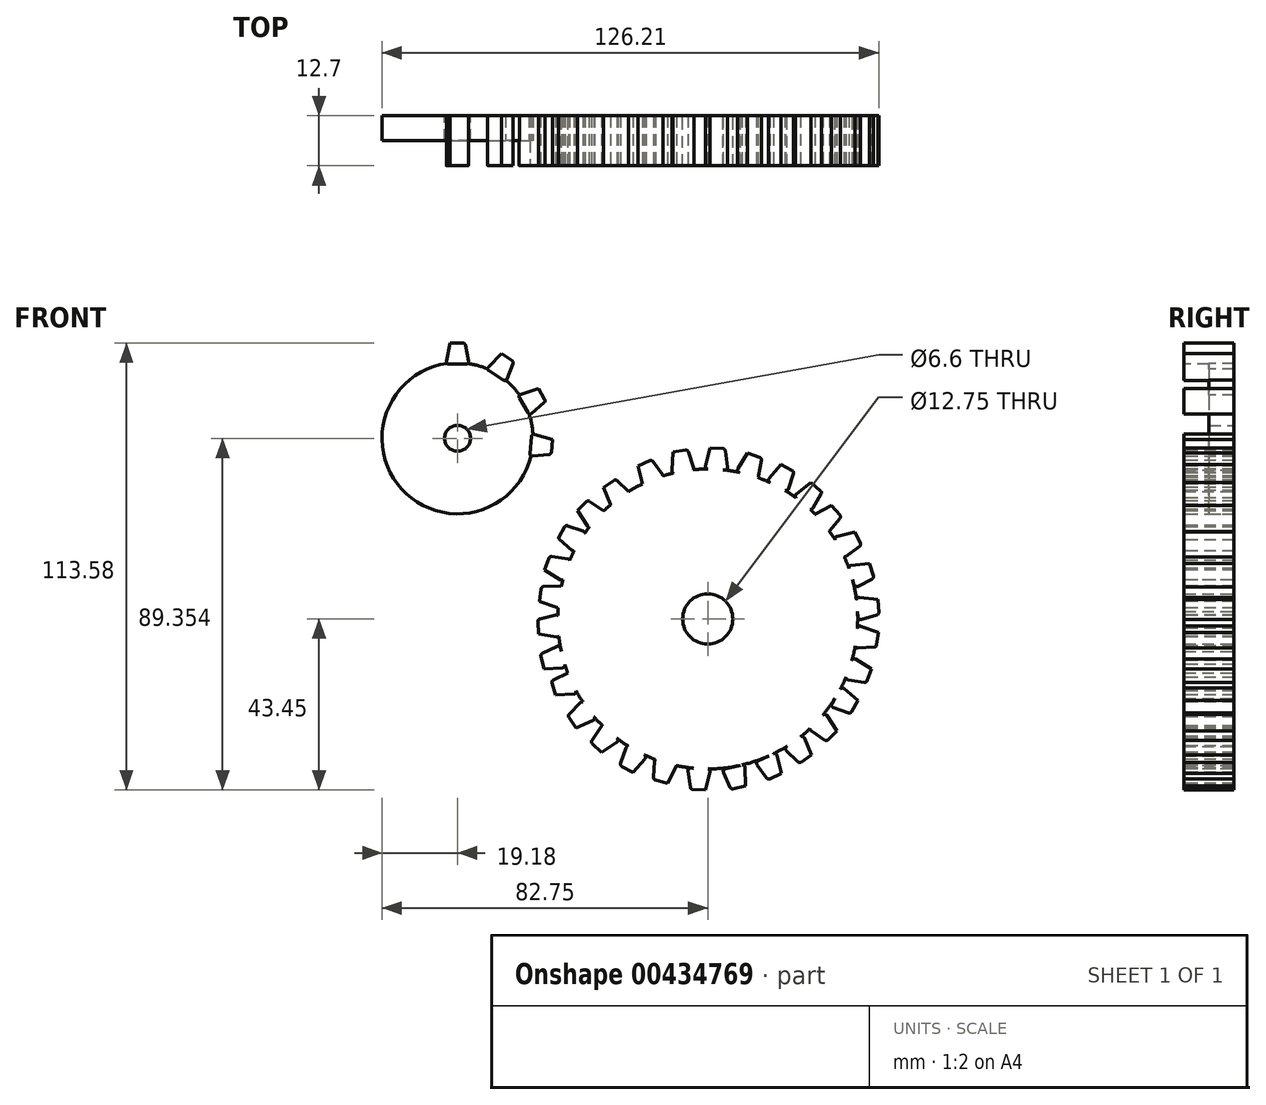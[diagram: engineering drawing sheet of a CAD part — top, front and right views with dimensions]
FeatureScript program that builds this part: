
annotation { "Feature Type Name" : "Feature", "Feature Type Description" : "" }
export const myFeature = defineFeature(function(context is Context, id is Id, definition is map)
    precondition{}
    {
        {
            var Q0;
            Q0=qCreatedBy(makeId("Front.planeOp"),FACE);
            var sketch = newSketch(context, id + "F0", { "sketchPlane" : qUnion([Q0])});
            skCircle(sketch, "E0", {"center": v(0, 0) * mm, "radius": 38.1 * mm});
            skCircle(sketch, "E1", {"center": v(0, 0) * mm, "radius": 6.37 * mm});
            skSolve(sketch);
        }
        {
            var Q0;
            Q0=makeQuery(id+"F0.imprint","IMPRINT",FACE,{"disambiguationData":[TD([[makeQuery(id+"F0.imprint","IMPRINT",EDGE,{"derivedFrom":sQuery(id+"F0.wireOp",EDGE,"E0")}),1.0]])]});
            extrude(context, id + "F1", {"entities" : qUnion([Q0]), "depth" : 12.7 * mm});
        }
        {
            var Q0;
            Q0=qCreatedBy(makeId("Front.planeOp"),FACE);
            var sketch = newSketch(context, id + "F2", { "sketchPlane" : qUnion([Q0])});
            skCircle(sketch, "E2", {"center": v(-63.57, 45.9) * mm, "radius": 19.18 * mm});
            skCircle(sketch, "E3", {"center": v(-63.57, 45.9) * mm, "radius": 3.3 * mm});
            skSolve(sketch);
        }
        {
            var Q0;
            Q0 = qSketchRegion(id + "F2", true);
            extrude(context, id + "F3", {"entities" : qUnion([Q0]), "depth" : 6.35 * mm});
        }
        {
            var Q0;
            Q0=makeQuery(id+"F1.opExtrude","CAP_FACE",FACE,{"disambiguationData":[OSD([sQuery(id+"F0.wireOp",EDGE,"E0"),sQuery(id+"F0.wireOp",EDGE,"E1")])],"isStart":false});
            var sketch = newSketch(context, id + "F4", { "sketchPlane" : qUnion([Q0])});
            skLineSegment(sketch, "E4", {"start": v(-6.97, 42.7) * mm, "end": v(-8.84, 42.45) * mm});
            skLineSegment(sketch, "E5", {"start": v(-8.84, 42.45) * mm, "end": v(-5.61, 42.9) * mm});
            skPoint(sketch, "E5.endSnap0", {"position": v(-7.9, 42.58) * mm});
            skLineSegment(sketch, "E6", {"start": v(-4.92, 42.47) * mm, "end": v(-3.6, 38.51) * mm});
            skLineSegment(sketch, "E7", {"start": v(-8.84, 42.45) * mm, "end": v(-9.14, 37.75) * mm});
            skLineSegment(sketch, "E8", {"start": v(-8.42, 37.08) * mm, "end": v(-4.1, 37.68) * mm});
            skPoint(sketch, "E9.visualSharp", {"position": v(-5.1, 42.96) * mm});
            skArc(sketch, "E9.filletArc", {"start": v(-4.92, 42.47) * mm, "mid": v(-5.2, 42.8) * mm, "end": v(-5.61, 42.9) * mm});
            skPoint(sketch, "E10.visualSharp", {"position": v(-3.35, 37.79) * mm});
            skArc(sketch, "E10.filletArc", {"start": v(-4.1, 37.68) * mm, "mid": v(-3.66, 37.98) * mm, "end": v(-3.6, 38.51) * mm});
            skPoint(sketch, "E11.visualSharp", {"position": v(-9.2, 36.97) * mm});
            skArc(sketch, "E11.filletArc", {"start": v(-9.14, 37.75) * mm, "mid": v(-8.94, 37.25) * mm, "end": v(-8.42, 37.08) * mm});
            skLineSegment(sketch, "E12", {"start": v(2.48, 43.35) * mm, "end": v(0.6, 43.45) * mm});
            skLineSegment(sketch, "E13", {"start": v(0.6, 43.45) * mm, "end": v(3.85, 43.28) * mm});
            skLineSegment(sketch, "E14", {"start": v(4.44, 42.73) * mm, "end": v(5, 38.6) * mm});
            skLineSegment(sketch, "E15", {"start": v(0.6, 43.45) * mm, "end": v(-0.58, 38.9) * mm});
            skLineSegment(sketch, "E16", {"start": v(0, 38.1) * mm, "end": v(4.35, 37.88) * mm});
            skArc(sketch, "E17.filletArc", {"start": v(4.44, 42.73) * mm, "mid": v(4.24, 43.12) * mm, "end": v(3.85, 43.28) * mm});
            skArc(sketch, "E18.filletArc", {"start": v(4.35, 37.88) * mm, "mid": v(4.85, 38.09) * mm, "end": v(5, 38.6) * mm});
            skArc(sketch, "E19.filletArc", {"start": v(-0.58, 38.9) * mm, "mid": v(-0.48, 38.36) * mm, "end": v(0, 38.1) * mm});
            skLineSegment(sketch, "E20", {"start": v(11.91, 41.54) * mm, "end": v(10.14, 42.19) * mm});
            skLineSegment(sketch, "E21", {"start": v(10.14, 42.19) * mm, "end": v(13.2, 41.08) * mm});
            skLineSegment(sketch, "E22", {"start": v(13.6, 40.38) * mm, "end": v(12.94, 36.26) * mm});
            skLineSegment(sketch, "E23", {"start": v(10.14, 42.19) * mm, "end": v(7.68, 38.18) * mm});
            skLineSegment(sketch, "E24", {"start": v(8, 37.25) * mm, "end": v(12.1, 35.77) * mm});
            skArc(sketch, "E25.filletArc", {"start": v(13.6, 40.38) * mm, "mid": v(13.53, 40.8) * mm, "end": v(13.2, 41.08) * mm});
            skArc(sketch, "E26.filletArc", {"start": v(12.1, 35.77) * mm, "mid": v(12.63, 35.81) * mm, "end": v(12.94, 36.26) * mm});
            skArc(sketch, "E27.filletArc", {"start": v(7.68, 38.18) * mm, "mid": v(7.62, 37.64) * mm, "end": v(8, 37.25) * mm});
            skLineSegment(sketch, "E28", {"start": v(27.62, 33.45) * mm, "end": v(26.18, 34.67) * mm});
            skLineSegment(sketch, "E29", {"start": v(26.18, 34.67) * mm, "end": v(28.66, 32.57) * mm});
            skLineSegment(sketch, "E30", {"start": v(28.8, 31.77) * mm, "end": v(26.76, 28.14) * mm});
            skLineSegment(sketch, "E31", {"start": v(26.18, 34.67) * mm, "end": v(22.48, 31.76) * mm});
            skLineSegment(sketch, "E32", {"start": v(22.47, 30.77) * mm, "end": v(25.8, 27.97) * mm});
            skArc(sketch, "E33.filletArc", {"start": v(28.8, 31.77) * mm, "mid": v(28.88, 32.2) * mm, "end": v(28.66, 32.57) * mm});
            skArc(sketch, "E34.filletArc", {"start": v(25.8, 27.97) * mm, "mid": v(26.32, 27.83) * mm, "end": v(26.76, 28.14) * mm});
            skArc(sketch, "E35.filletArc", {"start": v(22.48, 31.76) * mm, "mid": v(22.24, 31.27) * mm, "end": v(22.47, 30.77) * mm});
            skLineSegment(sketch, "E36", {"start": v(32.68, 27.4) * mm, "end": v(31.47, 28.85) * mm});
            skLineSegment(sketch, "E37", {"start": v(31.47, 28.85) * mm, "end": v(33.56, 26.36) * mm});
            skLineSegment(sketch, "E38", {"start": v(33.57, 25.55) * mm, "end": v(30.93, 22.32) * mm});
            skLineSegment(sketch, "E39", {"start": v(31.47, 28.85) * mm, "end": v(27.33, 26.61) * mm});
            skLineSegment(sketch, "E40", {"start": v(27.15, 25.65) * mm, "end": v(29.95, 22.31) * mm});
            skArc(sketch, "E41.filletArc", {"start": v(33.57, 25.55) * mm, "mid": v(33.71, 25.96) * mm, "end": v(33.56, 26.36) * mm});
            skArc(sketch, "E42.filletArc", {"start": v(29.95, 22.31) * mm, "mid": v(30.44, 22.09) * mm, "end": v(30.93, 22.32) * mm});
            skArc(sketch, "E43.filletArc", {"start": v(27.33, 26.61) * mm, "mid": v(27.01, 26.17) * mm, "end": v(27.15, 25.65) * mm});
            skLineSegment(sketch, "E44", {"start": v(38.16, 20.38) * mm, "end": v(37.37, 22.09) * mm});
            skLineSegment(sketch, "E45", {"start": v(37.37, 22.09) * mm, "end": v(38.74, 19.14) * mm});
            skLineSegment(sketch, "E46", {"start": v(38.54, 18.35) * mm, "end": v(35.15, 15.92) * mm});
            skLineSegment(sketch, "E47", {"start": v(37.37, 22.09) * mm, "end": v(32.79, 21) * mm});
            skLineSegment(sketch, "E48", {"start": v(32.36, 20.1) * mm, "end": v(34.2, 16.17) * mm});
            skArc(sketch, "E49.filletArc", {"start": v(38.54, 18.35) * mm, "mid": v(38.78, 18.7) * mm, "end": v(38.74, 19.14) * mm});
            skArc(sketch, "E50.filletArc", {"start": v(34.2, 16.17) * mm, "mid": v(34.62, 15.82) * mm, "end": v(35.15, 15.92) * mm});
            skArc(sketch, "E51.filletArc", {"start": v(32.79, 21) * mm, "mid": v(32.36, 20.65) * mm, "end": v(32.36, 20.1) * mm});
            skLineSegment(sketch, "E52", {"start": v(41.68, 12.28) * mm, "end": v(41.11, 14.08) * mm});
            skLineSegment(sketch, "E53", {"start": v(41.11, 14.08) * mm, "end": v(42.09, 10.97) * mm});
            skLineSegment(sketch, "E54", {"start": v(41.78, 10.22) * mm, "end": v(38.1, 8.26) * mm});
            skLineSegment(sketch, "E55", {"start": v(41.11, 14.08) * mm, "end": v(36.43, 13.6) * mm});
            skLineSegment(sketch, "E56", {"start": v(35.9, 12.78) * mm, "end": v(37.2, 8.63) * mm});
            skArc(sketch, "E57.filletArc", {"start": v(41.78, 10.22) * mm, "mid": v(42.07, 10.54) * mm, "end": v(42.09, 10.97) * mm});
            skArc(sketch, "E58.filletArc", {"start": v(37.2, 8.63) * mm, "mid": v(37.56, 8.23) * mm, "end": v(38.1, 8.26) * mm});
            skArc(sketch, "E59.filletArc", {"start": v(36.43, 13.6) * mm, "mid": v(35.97, 13.32) * mm, "end": v(35.9, 12.78) * mm});
            skLineSegment(sketch, "E60", {"start": v(43.34, 3.07) * mm, "end": v(43.18, 4.95) * mm});
            skLineSegment(sketch, "E61", {"start": v(43.18, 4.95) * mm, "end": v(43.46, 1.7) * mm});
            skLineSegment(sketch, "E62", {"start": v(43, 1.04) * mm, "end": v(38.99, -0.1) * mm});
            skLineSegment(sketch, "E63", {"start": v(43.18, 4.95) * mm, "end": v(38.5, 5.49) * mm});
            skLineSegment(sketch, "E64", {"start": v(37.8, 4.8) * mm, "end": v(38.18, 0.46) * mm});
            skArc(sketch, "E65.filletArc", {"start": v(43, 1.04) * mm, "mid": v(43.35, 1.29) * mm, "end": v(43.46, 1.7) * mm});
            skArc(sketch, "E66.filletArc", {"start": v(38.18, 0.46) * mm, "mid": v(38.45, 0) * mm, "end": v(38.99, -0.1) * mm});
            skArc(sketch, "E67.filletArc", {"start": v(38.5, 5.49) * mm, "mid": v(37.99, 5.3) * mm, "end": v(37.8, 4.8) * mm});
            skLineSegment(sketch, "E68", {"start": v(43.07, -5.26) * mm, "end": v(43.31, -3.4) * mm});
            skLineSegment(sketch, "E69", {"start": v(43.31, -3.4) * mm, "end": v(42.9, -6.62) * mm});
            skLineSegment(sketch, "E70", {"start": v(42.3, -7.17) * mm, "end": v(38.14, -7.42) * mm});
            skLineSegment(sketch, "E71", {"start": v(43.31, -3.4) * mm, "end": v(38.86, -1.87) * mm});
            skLineSegment(sketch, "E72", {"start": v(38.03, -2.39) * mm, "end": v(37.47, -6.7) * mm});
            skArc(sketch, "E73.filletArc", {"start": v(42.3, -7.17) * mm, "mid": v(42.7, -7) * mm, "end": v(42.9, -6.62) * mm});
            skArc(sketch, "E74.filletArc", {"start": v(37.47, -6.7) * mm, "mid": v(37.64, -7.22) * mm, "end": v(38.14, -7.42) * mm});
            skArc(sketch, "E75.filletArc", {"start": v(38.86, -1.87) * mm, "mid": v(38.32, -1.93) * mm, "end": v(38.03, -2.39) * mm});
            skLineSegment(sketch, "E76", {"start": v(40.91, -14.43) * mm, "end": v(41.56, -12.66) * mm});
            skLineSegment(sketch, "E77", {"start": v(41.56, -12.66) * mm, "end": v(40.45, -15.71) * mm});
            skLineSegment(sketch, "E78", {"start": v(39.75, -16.12) * mm, "end": v(35.63, -15.45) * mm});
            skLineSegment(sketch, "E79", {"start": v(41.56, -12.66) * mm, "end": v(37.55, -10.2) * mm});
            skLineSegment(sketch, "E80", {"start": v(36.62, -10.52) * mm, "end": v(35.14, -14.6) * mm});
            skArc(sketch, "E81.filletArc", {"start": v(39.75, -16.12) * mm, "mid": v(40.17, -16.04) * mm, "end": v(40.45, -15.71) * mm});
            skArc(sketch, "E82.filletArc", {"start": v(35.14, -14.6) * mm, "mid": v(35.18, -15.15) * mm, "end": v(35.63, -15.45) * mm});
            skArc(sketch, "E83.filletArc", {"start": v(37.55, -10.2) * mm, "mid": v(37, -10.13) * mm, "end": v(36.62, -10.52) * mm});
            skLineSegment(sketch, "E84", {"start": v(37.24, -22.38) * mm, "end": v(38.19, -20.75) * mm});
            skLineSegment(sketch, "E85", {"start": v(38.19, -20.75) * mm, "end": v(36.56, -23.57) * mm});
            skLineSegment(sketch, "E86", {"start": v(35.8, -23.85) * mm, "end": v(31.86, -22.47) * mm});
            skLineSegment(sketch, "E87", {"start": v(38.19, -20.75) * mm, "end": v(34.67, -17.63) * mm});
            skLineSegment(sketch, "E88", {"start": v(33.7, -17.78) * mm, "end": v(31.52, -21.56) * mm});
            skArc(sketch, "E89.filletArc", {"start": v(35.8, -23.85) * mm, "mid": v(36.23, -23.85) * mm, "end": v(36.56, -23.57) * mm});
            skArc(sketch, "E90.filletArc", {"start": v(31.52, -21.56) * mm, "mid": v(31.48, -22.1) * mm, "end": v(31.86, -22.47) * mm});
            skArc(sketch, "E91.filletArc", {"start": v(34.67, -17.63) * mm, "mid": v(34.14, -17.47) * mm, "end": v(33.7, -17.78) * mm});
            skLineSegment(sketch, "E92", {"start": v(31.5, -29.76) * mm, "end": v(32.83, -28.42) * mm});
            skLineSegment(sketch, "E93", {"start": v(32.83, -28.42) * mm, "end": v(30.53, -30.73) * mm});
            skLineSegment(sketch, "E94", {"start": v(29.73, -30.8) * mm, "end": v(26.28, -28.45) * mm});
            skLineSegment(sketch, "E95", {"start": v(32.83, -28.42) * mm, "end": v(30.24, -24.5) * mm});
            skLineSegment(sketch, "E96", {"start": v(29.26, -24.4) * mm, "end": v(26.19, -27.48) * mm});
            skArc(sketch, "E97.filletArc", {"start": v(29.73, -30.8) * mm, "mid": v(30.14, -30.9) * mm, "end": v(30.53, -30.73) * mm});
            skArc(sketch, "E98.filletArc", {"start": v(26.19, -27.48) * mm, "mid": v(26, -27.99) * mm, "end": v(26.28, -28.45) * mm});
            skArc(sketch, "E99.filletArc", {"start": v(30.24, -24.5) * mm, "mid": v(29.78, -24.21) * mm, "end": v(29.26, -24.4) * mm});
            skLineSegment(sketch, "E100", {"start": v(24.84, -35.6) * mm, "end": v(26.39, -34.52) * mm});
            skLineSegment(sketch, "E101", {"start": v(26.39, -34.52) * mm, "end": v(23.72, -36.39) * mm});
            skLineSegment(sketch, "E102", {"start": v(22.91, -36.32) * mm, "end": v(19.93, -33.41) * mm});
            skLineSegment(sketch, "E103", {"start": v(26.39, -34.52) * mm, "end": v(24.52, -30.2) * mm});
            skLineSegment(sketch, "E104", {"start": v(23.57, -29.94) * mm, "end": v(20, -32.44) * mm});
            skArc(sketch, "E105.filletArc", {"start": v(22.91, -36.32) * mm, "mid": v(23.3, -36.5) * mm, "end": v(23.72, -36.39) * mm});
            skArc(sketch, "E106.filletArc", {"start": v(20, -32.44) * mm, "mid": v(19.74, -32.9) * mm, "end": v(19.93, -33.41) * mm});
            skArc(sketch, "E107.filletArc", {"start": v(24.52, -30.2) * mm, "mid": v(24.1, -29.84) * mm, "end": v(23.57, -29.94) * mm});
            skLineSegment(sketch, "E108", {"start": v(16.98, -40.04) * mm, "end": v(18.7, -39.24) * mm});
            skLineSegment(sketch, "E109", {"start": v(18.7, -39.24) * mm, "end": v(15.74, -40.62) * mm});
            skLineSegment(sketch, "E110", {"start": v(14.96, -40.41) * mm, "end": v(12.52, -37.03) * mm});
            skLineSegment(sketch, "E111", {"start": v(18.7, -39.24) * mm, "end": v(17.6, -34.67) * mm});
            skLineSegment(sketch, "E112", {"start": v(16.71, -34.24) * mm, "end": v(12.77, -36.08) * mm});
            skArc(sketch, "E113.filletArc", {"start": v(14.96, -40.41) * mm, "mid": v(15.31, -40.66) * mm, "end": v(15.74, -40.62) * mm});
            skArc(sketch, "E114.filletArc", {"start": v(12.77, -36.08) * mm, "mid": v(12.42, -36.5) * mm, "end": v(12.52, -37.03) * mm});
            skArc(sketch, "E115.filletArc", {"start": v(17.6, -34.67) * mm, "mid": v(17.26, -34.24) * mm, "end": v(16.71, -34.24) * mm});
            skLineSegment(sketch, "E116", {"start": v(7.7, -42.83) * mm, "end": v(9.54, -42.41) * mm});
            skLineSegment(sketch, "E117", {"start": v(9.54, -42.41) * mm, "end": v(6.37, -43.13) * mm});
            skLineSegment(sketch, "E118", {"start": v(5.65, -42.77) * mm, "end": v(3.98, -38.94) * mm});
            skLineSegment(sketch, "E119", {"start": v(9.54, -42.41) * mm, "end": v(9.44, -37.7) * mm});
            skLineSegment(sketch, "E120", {"start": v(8.67, -37.1) * mm, "end": v(4.42, -38.07) * mm});
            skArc(sketch, "E121.filletArc", {"start": v(5.65, -42.77) * mm, "mid": v(5.94, -43.08) * mm, "end": v(6.37, -43.13) * mm});
            skArc(sketch, "E122.filletArc", {"start": v(4.42, -38.07) * mm, "mid": v(4, -38.4) * mm, "end": v(3.98, -38.94) * mm});
            skArc(sketch, "E123.filletArc", {"start": v(9.44, -37.7) * mm, "mid": v(9.2, -37.22) * mm, "end": v(8.67, -37.1) * mm});
            skLineSegment(sketch, "E124", {"start": v(-2.47, -43.36) * mm, "end": v(-0.59, -43.45) * mm});
            skLineSegment(sketch, "E125", {"start": v(-0.59, -43.45) * mm, "end": v(-3.84, -43.3) * mm});
            skLineSegment(sketch, "E126", {"start": v(-4.43, -42.74) * mm, "end": v(-5, -38.61) * mm});
            skLineSegment(sketch, "E127", {"start": v(-0.59, -43.45) * mm, "end": v(0.58, -38.9) * mm});
            skLineSegment(sketch, "E128", {"start": v(0, -38.1) * mm, "end": v(-4.35, -37.9) * mm});
            skArc(sketch, "E129.filletArc", {"start": v(-4.43, -42.74) * mm, "mid": v(-4.23, -43.12) * mm, "end": v(-3.84, -43.3) * mm});
            skArc(sketch, "E130.filletArc", {"start": v(-4.35, -37.9) * mm, "mid": v(-4.85, -38.1) * mm, "end": v(-5, -38.61) * mm});
            skArc(sketch, "E131.filletArc", {"start": v(0.58, -38.9) * mm, "mid": v(0.48, -38.36) * mm, "end": v(0, -38.1) * mm});
            skLineSegment(sketch, "E132", {"start": v(-12, -41.27) * mm, "end": v(-10.17, -41.75) * mm});
            skLineSegment(sketch, "E133", {"start": v(-10.17, -41.75) * mm, "end": v(-13.32, -40.91) * mm});
            skLineSegment(sketch, "E134", {"start": v(-13.79, -40.25) * mm, "end": v(-13.48, -36.1) * mm});
            skLineSegment(sketch, "E135", {"start": v(-10.17, -41.75) * mm, "end": v(-8.07, -37.55) * mm});
            skLineSegment(sketch, "E136", {"start": v(-8.47, -36.65) * mm, "end": v(-12.68, -35.53) * mm});
            skArc(sketch, "E137.filletArc", {"start": v(-13.79, -40.25) * mm, "mid": v(-13.67, -40.67) * mm, "end": v(-13.32, -40.91) * mm});
            skArc(sketch, "E138.filletArc", {"start": v(-12.68, -35.53) * mm, "mid": v(-13.21, -35.62) * mm, "end": v(-13.48, -36.1) * mm});
            skArc(sketch, "E139.filletArc", {"start": v(-8.07, -37.55) * mm, "mid": v(-8.06, -37) * mm, "end": v(-8.47, -36.65) * mm});
            skLineSegment(sketch, "E140", {"start": v(-20.67, -38.1) * mm, "end": v(-19.04, -39.04) * mm});
            skLineSegment(sketch, "E141", {"start": v(-19.04, -39.04) * mm, "end": v(-21.86, -37.4) * mm});
            skLineSegment(sketch, "E142", {"start": v(-22.14, -36.65) * mm, "end": v(-20.76, -32.71) * mm});
            skLineSegment(sketch, "E143", {"start": v(-19.04, -39.04) * mm, "end": v(-15.91, -35.52) * mm});
            skLineSegment(sketch, "E144", {"start": v(-16.07, -34.54) * mm, "end": v(-19.84, -32.37) * mm});
            skArc(sketch, "E145.filletArc", {"start": v(-22.14, -36.65) * mm, "mid": v(-22.13, -37.08) * mm, "end": v(-21.86, -37.4) * mm});
            skArc(sketch, "E146.filletArc", {"start": v(-19.84, -32.37) * mm, "mid": v(-20.38, -32.33) * mm, "end": v(-20.76, -32.71) * mm});
            skArc(sketch, "E147.filletArc", {"start": v(-15.91, -35.52) * mm, "mid": v(-15.76, -35) * mm, "end": v(-16.07, -34.54) * mm});
            skLineSegment(sketch, "E148", {"start": v(-28.39, -32.6) * mm, "end": v(-27.05, -33.92) * mm});
            skLineSegment(sketch, "E149", {"start": v(-27.05, -33.92) * mm, "end": v(-29.36, -31.62) * mm});
            skLineSegment(sketch, "E150", {"start": v(-29.43, -30.82) * mm, "end": v(-27.08, -27.37) * mm});
            skLineSegment(sketch, "E151", {"start": v(-27.05, -33.92) * mm, "end": v(-23.13, -31.33) * mm});
            skLineSegment(sketch, "E152", {"start": v(-23.03, -30.35) * mm, "end": v(-26.1, -27.28) * mm});
            skArc(sketch, "E153.filletArc", {"start": v(-29.43, -30.82) * mm, "mid": v(-29.54, -31.23) * mm, "end": v(-29.36, -31.62) * mm});
            skArc(sketch, "E154.filletArc", {"start": v(-26.1, -27.28) * mm, "mid": v(-26.62, -27.1) * mm, "end": v(-27.08, -27.37) * mm});
            skArc(sketch, "E155.filletArc", {"start": v(-23.13, -31.33) * mm, "mid": v(-22.84, -30.87) * mm, "end": v(-23.03, -30.35) * mm});
            skLineSegment(sketch, "E156", {"start": v(-34.53, -26.15) * mm, "end": v(-33.44, -27.7) * mm});
            skLineSegment(sketch, "E157", {"start": v(-33.44, -27.7) * mm, "end": v(-35.31, -25.03) * mm});
            skLineSegment(sketch, "E158", {"start": v(-35.24, -24.22) * mm, "end": v(-32.33, -21.23) * mm});
            skLineSegment(sketch, "E159", {"start": v(-33.44, -27.7) * mm, "end": v(-29.13, -25.82) * mm});
            skLineSegment(sketch, "E160", {"start": v(-28.86, -24.88) * mm, "end": v(-31.36, -21.31) * mm});
            skArc(sketch, "E161.filletArc", {"start": v(-35.24, -24.22) * mm, "mid": v(-35.42, -24.61) * mm, "end": v(-35.31, -25.03) * mm});
            skArc(sketch, "E162.filletArc", {"start": v(-31.36, -21.31) * mm, "mid": v(-31.83, -21.04) * mm, "end": v(-32.33, -21.23) * mm});
            skArc(sketch, "E163.filletArc", {"start": v(-29.13, -25.82) * mm, "mid": v(-28.77, -25.41) * mm, "end": v(-28.86, -24.88) * mm});
            skLineSegment(sketch, "E164", {"start": v(-15.98, 39.67) * mm, "end": v(-17.69, 38.87) * mm});
            skLineSegment(sketch, "E165", {"start": v(-17.69, 38.87) * mm, "end": v(-14.74, 40.25) * mm});
            skLineSegment(sketch, "E166", {"start": v(-13.96, 40.04) * mm, "end": v(-11.52, 36.66) * mm});
            skLineSegment(sketch, "E167", {"start": v(-17.69, 38.87) * mm, "end": v(-16.6, 34.3) * mm});
            skLineSegment(sketch, "E168", {"start": v(-15.71, 33.87) * mm, "end": v(-11.77, 35.71) * mm});
            skArc(sketch, "E169.filletArc", {"start": v(-13.96, 40.04) * mm, "mid": v(-14.31, 40.29) * mm, "end": v(-14.74, 40.25) * mm});
            skArc(sketch, "E170.filletArc", {"start": v(-11.77, 35.71) * mm, "mid": v(-11.42, 36.13) * mm, "end": v(-11.52, 36.66) * mm});
            skArc(sketch, "E171.filletArc", {"start": v(-16.6, 34.3) * mm, "mid": v(-16.26, 33.87) * mm, "end": v(-15.71, 33.87) * mm});
            skLineSegment(sketch, "E172", {"start": v(-24.98, 34.45) * mm, "end": v(-26.52, 33.37) * mm});
            skLineSegment(sketch, "E173", {"start": v(-26.52, 33.37) * mm, "end": v(-23.86, 35.23) * mm});
            skLineSegment(sketch, "E174", {"start": v(-23.05, 35.17) * mm, "end": v(-20.06, 32.26) * mm});
            skLineSegment(sketch, "E175", {"start": v(-26.52, 33.37) * mm, "end": v(-24.65, 29.05) * mm});
            skLineSegment(sketch, "E176", {"start": v(-23.7, 28.78) * mm, "end": v(-20.14, 31.28) * mm});
            skArc(sketch, "E177.filletArc", {"start": v(-23.05, 35.17) * mm, "mid": v(-23.44, 35.35) * mm, "end": v(-23.86, 35.23) * mm});
            skArc(sketch, "E178.filletArc", {"start": v(-20.14, 31.28) * mm, "mid": v(-19.87, 31.75) * mm, "end": v(-20.06, 32.26) * mm});
            skArc(sketch, "E179.filletArc", {"start": v(-24.65, 29.05) * mm, "mid": v(-24.24, 28.7) * mm, "end": v(-23.7, 28.78) * mm});
            skLineSegment(sketch, "E180", {"start": v(-40.79, 14.19) * mm, "end": v(-41.43, 12.42) * mm});
            skLineSegment(sketch, "E181", {"start": v(-41.43, 12.42) * mm, "end": v(-40.32, 15.47) * mm});
            skLineSegment(sketch, "E182", {"start": v(-39.62, 15.88) * mm, "end": v(-35.5, 15.21) * mm});
            skLineSegment(sketch, "E183", {"start": v(-41.43, 12.42) * mm, "end": v(-37.43, 9.95) * mm});
            skLineSegment(sketch, "E184", {"start": v(-36.5, 10.28) * mm, "end": v(-35.01, 14.37) * mm});
            skArc(sketch, "E185.filletArc", {"start": v(-39.62, 15.88) * mm, "mid": v(-40.05, 15.8) * mm, "end": v(-40.32, 15.47) * mm});
            skArc(sketch, "E186.filletArc", {"start": v(-35.01, 14.37) * mm, "mid": v(-35.06, 14.9) * mm, "end": v(-35.5, 15.21) * mm});
            skArc(sketch, "E187.filletArc", {"start": v(-37.43, 9.95) * mm, "mid": v(-36.88, 9.9) * mm, "end": v(-36.5, 10.28) * mm});
            skLineSegment(sketch, "E188", {"start": v(-42.53, 6.3) * mm, "end": v(-42.79, 4.43) * mm});
            skLineSegment(sketch, "E189", {"start": v(-42.79, 4.43) * mm, "end": v(-42.34, 7.66) * mm});
            skLineSegment(sketch, "E190", {"start": v(-41.74, 8.2) * mm, "end": v(-37.58, 8.4) * mm});
            skLineSegment(sketch, "E191", {"start": v(-42.79, 4.43) * mm, "end": v(-38.35, 2.86) * mm});
            skLineSegment(sketch, "E192", {"start": v(-37.51, 3.38) * mm, "end": v(-36.92, 7.69) * mm});
            skArc(sketch, "E193.filletArc", {"start": v(-41.74, 8.2) * mm, "mid": v(-42.14, 8.04) * mm, "end": v(-42.34, 7.66) * mm});
            skArc(sketch, "E194.filletArc", {"start": v(-36.92, 7.69) * mm, "mid": v(-37.08, 8.2) * mm, "end": v(-37.58, 8.4) * mm});
            skArc(sketch, "E195.filletArc", {"start": v(-38.35, 2.86) * mm, "mid": v(-37.8, 2.92) * mm, "end": v(-37.51, 3.38) * mm});
            skLineSegment(sketch, "E196", {"start": v(-39.2, -17.53) * mm, "end": v(-38.7, -19.35) * mm});
            skLineSegment(sketch, "E197", {"start": v(-38.7, -19.35) * mm, "end": v(-39.55, -16.2) * mm});
            skLineSegment(sketch, "E198", {"start": v(-39.2, -15.47) * mm, "end": v(-35.45, -13.66) * mm});
            skLineSegment(sketch, "E199", {"start": v(-38.7, -19.35) * mm, "end": v(-34, -19.07) * mm});
            skLineSegment(sketch, "E200", {"start": v(-33.43, -18.27) * mm, "end": v(-34.56, -14.07) * mm});
            skArc(sketch, "E201.filletArc", {"start": v(-39.2, -15.47) * mm, "mid": v(-39.51, -15.78) * mm, "end": v(-39.55, -16.2) * mm});
            skArc(sketch, "E202.filletArc", {"start": v(-34.56, -14.07) * mm, "mid": v(-34.91, -13.66) * mm, "end": v(-35.45, -13.66) * mm});
            skArc(sketch, "E203.filletArc", {"start": v(-34, -19.07) * mm, "mid": v(-33.53, -18.8) * mm, "end": v(-33.43, -18.27) * mm});
            skLineSegment(sketch, "E204", {"start": v(-42.06, -10.84) * mm, "end": v(-41.57, -12.66) * mm});
            skLineSegment(sketch, "E205", {"start": v(-41.57, -12.66) * mm, "end": v(-42.41, -9.52) * mm});
            skLineSegment(sketch, "E206", {"start": v(-42.07, -8.78) * mm, "end": v(-38.32, -6.97) * mm});
            skLineSegment(sketch, "E207", {"start": v(-41.57, -12.66) * mm, "end": v(-36.87, -12.38) * mm});
            skLineSegment(sketch, "E208", {"start": v(-36.3, -11.58) * mm, "end": v(-37.43, -7.38) * mm});
            skArc(sketch, "E209.filletArc", {"start": v(-42.07, -8.78) * mm, "mid": v(-42.38, -9.1) * mm, "end": v(-42.41, -9.52) * mm});
            skArc(sketch, "E210.filletArc", {"start": v(-37.43, -7.38) * mm, "mid": v(-37.78, -6.97) * mm, "end": v(-38.32, -6.97) * mm});
            skArc(sketch, "E211.filletArc", {"start": v(-36.87, -12.38) * mm, "mid": v(-36.4, -12.12) * mm, "end": v(-36.3, -11.58) * mm});
            skLineSegment(sketch, "E212", {"start": v(-43.09, -1.96) * mm, "end": v(-43, -3.85) * mm});
            skLineSegment(sketch, "E213", {"start": v(-43, -3.85) * mm, "end": v(-43.14, -0.6) * mm});
            skLineSegment(sketch, "E214", {"start": v(-42.65, 0.05) * mm, "end": v(-38.59, 0.99) * mm});
            skLineSegment(sketch, "E215", {"start": v(-43, -3.85) * mm, "end": v(-38.37, -4.6) * mm});
            skLineSegment(sketch, "E216", {"start": v(-37.63, -3.95) * mm, "end": v(-37.8, 0.4) * mm});
            skArc(sketch, "E217.filletArc", {"start": v(-42.65, 0.05) * mm, "mid": v(-43.01, -0.18) * mm, "end": v(-43.14, -0.6) * mm});
            skArc(sketch, "E218.filletArc", {"start": v(-37.8, 0.4) * mm, "mid": v(-38.06, 0.88) * mm, "end": v(-38.59, 0.99) * mm});
            skArc(sketch, "E219.filletArc", {"start": v(-38.37, -4.6) * mm, "mid": v(-37.84, -4.45) * mm, "end": v(-37.63, -3.95) * mm});
            skLineSegment(sketch, "E220.0", {"start": v(-7.9, 42.58) * mm, "end": v(-5.1, 42.96) * mm, "construction": true});
            skLineSegment(sketch, "E221", {"start": v(20.23, 38.4) * mm, "end": v(18.56, 39.28) * mm});
            skLineSegment(sketch, "E222", {"start": v(18.56, 39.28) * mm, "end": v(21.44, 37.77) * mm});
            skLineSegment(sketch, "E223", {"start": v(21.75, 37.02) * mm, "end": v(20.53, 33.03) * mm});
            skLineSegment(sketch, "E224", {"start": v(18.56, 39.28) * mm, "end": v(15.58, 35.65) * mm});
            skLineSegment(sketch, "E225", {"start": v(15.77, 34.68) * mm, "end": v(19.62, 32.66) * mm});
            skArc(sketch, "E226.filletArc", {"start": v(21.75, 37.02) * mm, "mid": v(21.73, 37.45) * mm, "end": v(21.44, 37.77) * mm});
            skArc(sketch, "E227.filletArc", {"start": v(19.62, 32.66) * mm, "mid": v(20.16, 32.63) * mm, "end": v(20.53, 33.03) * mm});
            skArc(sketch, "E228.filletArc", {"start": v(15.58, 35.65) * mm, "mid": v(15.44, 35.12) * mm, "end": v(15.77, 34.68) * mm});
            skLineSegment(sketch, "E229", {"start": v(-31.8, 28.85) * mm, "end": v(-33.14, 27.51) * mm});
            skLineSegment(sketch, "E230", {"start": v(-33.14, 27.51) * mm, "end": v(-30.84, 29.81) * mm});
            skLineSegment(sketch, "E231", {"start": v(-30.04, 29.89) * mm, "end": v(-26.59, 27.54) * mm});
            skLineSegment(sketch, "E232", {"start": v(-33.14, 27.51) * mm, "end": v(-30.55, 23.59) * mm});
            skLineSegment(sketch, "E233", {"start": v(-29.57, 23.49) * mm, "end": v(-26.5, 26.57) * mm});
            skArc(sketch, "E234.filletArc", {"start": v(-30.04, 29.89) * mm, "mid": v(-30.45, 30) * mm, "end": v(-30.84, 29.81) * mm});
            skArc(sketch, "E235.filletArc", {"start": v(-26.5, 26.57) * mm, "mid": v(-26.31, 27.08) * mm, "end": v(-26.59, 27.54) * mm});
            skArc(sketch, "E236.filletArc", {"start": v(-30.55, 23.59) * mm, "mid": v(-30.08, 23.3) * mm, "end": v(-29.57, 23.49) * mm});
            skLineSegment(sketch, "E237", {"start": v(-37.82, 20.86) * mm, "end": v(-36.36, 23.39) * mm});
            skLineSegment(sketch, "E238", {"start": v(-35.6, 23.67) * mm, "end": v(-31.66, 22.3) * mm});
            skLineSegment(sketch, "E239", {"start": v(-37.74, 20.35) * mm, "end": v(-34.46, 17.45) * mm});
            skLineSegment(sketch, "E240", {"start": v(-33.5, 17.6) * mm, "end": v(-31.32, 21.38) * mm});
            skArc(sketch, "E241.filletArc", {"start": v(-35.6, 23.67) * mm, "mid": v(-36.03, 23.67) * mm, "end": v(-36.36, 23.39) * mm});
            skArc(sketch, "E242.filletArc", {"start": v(-31.32, 21.38) * mm, "mid": v(-31.27, 21.92) * mm, "end": v(-31.66, 22.3) * mm});
            skArc(sketch, "E243.filletArc", {"start": v(-34.46, 17.45) * mm, "mid": v(-33.94, 17.3) * mm, "end": v(-33.5, 17.6) * mm});
            skArc(sketch, "E244.filletArc", {"start": v(-37.82, 20.86) * mm, "mid": v(-37.87, 20.6) * mm, "end": v(-37.74, 20.35) * mm});
            skPoint(sketch, "E245.visualSharp", {"position": v(-37.82, 20.86) * mm});
            skLineSegment(sketch, "E245.filletArc", {"start": v(-37.82, 20.86) * mm, "end": v(-37.82, 20.86) * mm});
            skSolve(sketch);
        }
        {
            var Q0;
            {var subQ7=sQuery(id+"F4.wireOp",EDGE,"E6");Q0=makeQuery(id+"F4.imprint","IMPRINT",FACE,{"disambiguationData":[TD([[makeQuery(id+"F4.imprint","IMPRINT",EDGE,{"derivedFrom":subQ7}),-1.0]])]});}
            var Q1;
            Q1=makeQuery(id+"F4.imprint","IMPRINT",FACE,{"disambiguationData":[TD([[makeQuery(id+"F4.imprint","IMPRINT",EDGE,{"derivedFrom":sQuery(id+"F4.wireOp",EDGE,"E14")}),-1.0]])]});
            var Q2;
            {var subQ6=sQuery(id+"F4.wireOp",EDGE,"E22");Q2=makeQuery(id+"F4.imprint","IMPRINT",FACE,{"disambiguationData":[TD([[makeQuery(id+"F4.imprint","IMPRINT",EDGE,{"derivedFrom":subQ6}),-1.0]])]});}
            var Q3;
            {var subQ2=sQuery(id+"F4.wireOp",EDGE,"E30");Q3=makeQuery(id+"F4.imprint","IMPRINT",FACE,{"disambiguationData":[TD([[makeQuery(id+"F4.imprint","IMPRINT",EDGE,{"derivedFrom":subQ2}),-1.0]])]});}
            var Q4;
            {var subQ2=sQuery(id+"F4.wireOp",EDGE,"E38");Q4=makeQuery(id+"F4.imprint","IMPRINT",FACE,{"disambiguationData":[TD([[makeQuery(id+"F4.imprint","IMPRINT",EDGE,{"derivedFrom":subQ2}),-1.0]])]});}
            var Q5;
            {var subQ2=sQuery(id+"F4.wireOp",EDGE,"E46");Q5=makeQuery(id+"F4.imprint","IMPRINT",FACE,{"disambiguationData":[TD([[makeQuery(id+"F4.imprint","IMPRINT",EDGE,{"derivedFrom":subQ2}),-1.0]])]});}
            var Q6;
            Q6=makeQuery(id+"F4.imprint","IMPRINT",FACE,{"disambiguationData":[TD([[makeQuery(id+"F4.imprint","IMPRINT",EDGE,{"derivedFrom":sQuery(id+"F4.wireOp",EDGE,"E54")}),-1.0]])]});
            var Q7;
            Q7=makeQuery(id+"F4.imprint","IMPRINT",FACE,{"disambiguationData":[TD([[makeQuery(id+"F4.imprint","IMPRINT",EDGE,{"derivedFrom":sQuery(id+"F4.wireOp",EDGE,"E62")}),-1.0]])]});
            var Q8;
            {var subQ6=sQuery(id+"F4.wireOp",EDGE,"E70");Q8=makeQuery(id+"F4.imprint","IMPRINT",FACE,{"disambiguationData":[TD([[makeQuery(id+"F4.imprint","IMPRINT",EDGE,{"derivedFrom":subQ6}),-1.0]])]});}
            var Q9;
            {var subQ2=sQuery(id+"F4.wireOp",EDGE,"E78");Q9=makeQuery(id+"F4.imprint","IMPRINT",FACE,{"disambiguationData":[TD([[makeQuery(id+"F4.imprint","IMPRINT",EDGE,{"derivedFrom":subQ2}),-1.0]])]});}
            var Q10;
            Q10=makeQuery(id+"F4.imprint","IMPRINT",FACE,{"disambiguationData":[TD([[makeQuery(id+"F4.imprint","IMPRINT",EDGE,{"derivedFrom":sQuery(id+"F4.wireOp",EDGE,"E86")}),-1.0]])]});
            var Q11;
            {var subQ2=sQuery(id+"F4.wireOp",EDGE,"E94");Q11=makeQuery(id+"F4.imprint","IMPRINT",FACE,{"disambiguationData":[TD([[makeQuery(id+"F4.imprint","IMPRINT",EDGE,{"derivedFrom":subQ2}),-1.0]])]});}
            var Q12;
            Q12=makeQuery(id+"F4.imprint","IMPRINT",FACE,{"disambiguationData":[TD([[makeQuery(id+"F4.imprint","IMPRINT",EDGE,{"derivedFrom":sQuery(id+"F4.wireOp",EDGE,"E102")}),-1.0]])]});
            var Q13;
            Q13=makeQuery(id+"F4.imprint","IMPRINT",FACE,{"disambiguationData":[TD([[makeQuery(id+"F4.imprint","IMPRINT",EDGE,{"derivedFrom":sQuery(id+"F4.wireOp",EDGE,"E110")}),-1.0]])]});
            var Q14;
            Q14=makeQuery(id+"F4.imprint","IMPRINT",FACE,{"disambiguationData":[TD([[makeQuery(id+"F4.imprint","IMPRINT",EDGE,{"derivedFrom":sQuery(id+"F4.wireOp",EDGE,"E118")}),-1.0]])]});
            var Q15;
            Q15=makeQuery(id+"F4.imprint","IMPRINT",FACE,{"disambiguationData":[TD([[makeQuery(id+"F4.imprint","IMPRINT",EDGE,{"derivedFrom":sQuery(id+"F4.wireOp",EDGE,"E126")}),-1.0]])]});
            var Q16;
            {var subQ2=sQuery(id+"F4.wireOp",EDGE,"E134");Q16=makeQuery(id+"F4.imprint","IMPRINT",FACE,{"disambiguationData":[TD([[makeQuery(id+"F4.imprint","IMPRINT",EDGE,{"derivedFrom":subQ2}),-1.0]])]});}
            var Q17;
            {var subQ2=sQuery(id+"F4.wireOp",EDGE,"E142");Q17=makeQuery(id+"F4.imprint","IMPRINT",FACE,{"disambiguationData":[TD([[makeQuery(id+"F4.imprint","IMPRINT",EDGE,{"derivedFrom":subQ2}),-1.0]])]});}
            var Q18;
            {var subQ2=sQuery(id+"F4.wireOp",EDGE,"E150");Q18=makeQuery(id+"F4.imprint","IMPRINT",FACE,{"disambiguationData":[TD([[makeQuery(id+"F4.imprint","IMPRINT",EDGE,{"derivedFrom":subQ2}),-1.0]])]});}
            var Q19;
            {var subQ2=sQuery(id+"F4.wireOp",EDGE,"E158");Q19=makeQuery(id+"F4.imprint","IMPRINT",FACE,{"disambiguationData":[TD([[makeQuery(id+"F4.imprint","IMPRINT",EDGE,{"derivedFrom":subQ2}),-1.0]])]});}
            var Q20;
            {var subQ5=sQuery(id+"F4.wireOp",EDGE,"E166");Q20=makeQuery(id+"F4.imprint","IMPRINT",FACE,{"disambiguationData":[TD([[makeQuery(id+"F4.imprint","IMPRINT",EDGE,{"derivedFrom":subQ5}),-1.0]])]});}
            var Q21;
            {var subQ0=sQuery(id+"F4.wireOp",EDGE,"E175");Q21=makeQuery(id+"F4.imprint","IMPRINT",FACE,{"disambiguationData":[TD([[makeQuery(id+"F4.imprint","IMPRINT",EDGE,{"derivedFrom":subQ0}),1.0]])]});}
            var Q22;
            {var subQ7=sQuery(id+"F4.wireOp",EDGE,"E182");Q22=makeQuery(id+"F4.imprint","IMPRINT",FACE,{"disambiguationData":[TD([[makeQuery(id+"F4.imprint","IMPRINT",EDGE,{"derivedFrom":subQ7}),-1.0]])]});}
            var Q23;
            {var subQ2=sQuery(id+"F4.wireOp",EDGE,"E190");Q23=makeQuery(id+"F4.imprint","IMPRINT",FACE,{"disambiguationData":[TD([[makeQuery(id+"F4.imprint","IMPRINT",EDGE,{"derivedFrom":subQ2}),-1.0]])]});}
            var Q24;
            {var subQ0=sQuery(id+"F4.wireOp",EDGE,"E199");Q24=makeQuery(id+"F4.imprint","IMPRINT",FACE,{"disambiguationData":[TD([[makeQuery(id+"F4.imprint","IMPRINT",EDGE,{"derivedFrom":subQ0}),1.0]])]});}
            var Q25;
            Q25=makeQuery(id+"F4.imprint","IMPRINT",FACE,{"disambiguationData":[TD([[makeQuery(id+"F4.imprint","IMPRINT",EDGE,{"derivedFrom":sQuery(id+"F4.wireOp",EDGE,"E206")}),-1.0]])]});
            var Q26;
            {var subQ2=sQuery(id+"F4.wireOp",EDGE,"E214");Q26=makeQuery(id+"F4.imprint","IMPRINT",FACE,{"disambiguationData":[TD([[makeQuery(id+"F4.imprint","IMPRINT",EDGE,{"derivedFrom":subQ2}),-1.0]])]});}
            var Q27;
            {var subQ6=sQuery(id+"F4.wireOp",EDGE,"E223");Q27=makeQuery(id+"F4.imprint","IMPRINT",FACE,{"disambiguationData":[TD([[makeQuery(id+"F4.imprint","IMPRINT",EDGE,{"derivedFrom":subQ6}),-1.0]])]});}
            var Q28;
            {var subQ2=sQuery(id+"F4.wireOp",EDGE,"E231");Q28=makeQuery(id+"F4.imprint","IMPRINT",FACE,{"disambiguationData":[TD([[makeQuery(id+"F4.imprint","IMPRINT",EDGE,{"derivedFrom":subQ2}),-1.0]])]});}
            var Q29;
            {var subQ0=sQuery(id+"F4.wireOp",EDGE,"E8");Q29=makeQuery(id+"F4.imprint","IMPRINT",FACE,{"disambiguationData":[TD([[makeQuery(id+"F4.imprint","IMPRINT",EDGE,{"derivedFrom":subQ0}),1.0]])]});}
            var Q30;
            {var subQ0=sQuery(id+"F4.wireOp",EDGE,"E16");var subQ1=makeQuery(id+"F1.opExtrude","CAP_EDGE",EDGE,{"disambiguationData":[OSD([sQuery(id+"F0.wireOp",EDGE,"E0")])],"isStart":false});var subQ3=makeQuery(id+"F4.imprint","INTERSECT",VERTEX,{"derivedFrom":[subQ1,subQ0]});Q30=makeQuery(id+"F4.imprint","IMPRINT",FACE,{"disambiguationData":[TD([[makeQuery(id+"F4.imprint","IMPRINT",EDGE,{"disambiguationData":[TD([[subQ3,1.0]])],"derivedFrom":subQ0}),1.0]])]});}
            var Q31;
            {var subQ0=sQuery(id+"F4.wireOp",EDGE,"E24");Q31=makeQuery(id+"F4.imprint","IMPRINT",FACE,{"disambiguationData":[TD([[makeQuery(id+"F4.imprint","IMPRINT",EDGE,{"derivedFrom":subQ0}),1.0]])]});}
            var Q32;
            {var subQ0=sQuery(id+"F4.wireOp",EDGE,"E32");Q32=makeQuery(id+"F4.imprint","IMPRINT",FACE,{"disambiguationData":[TD([[makeQuery(id+"F4.imprint","IMPRINT",EDGE,{"derivedFrom":subQ0}),1.0]])]});}
            var Q33;
            {var subQ0=sQuery(id+"F4.wireOp",EDGE,"E40");Q33=makeQuery(id+"F4.imprint","IMPRINT",FACE,{"disambiguationData":[TD([[makeQuery(id+"F4.imprint","IMPRINT",EDGE,{"derivedFrom":subQ0}),1.0]])]});}
            var Q34;
            {var subQ0=sQuery(id+"F4.wireOp",EDGE,"E48");Q34=makeQuery(id+"F4.imprint","IMPRINT",FACE,{"disambiguationData":[TD([[makeQuery(id+"F4.imprint","IMPRINT",EDGE,{"derivedFrom":subQ0}),1.0]])]});}
            var Q35;
            {var subQ0=sQuery(id+"F4.wireOp",EDGE,"E56");var subQ1=makeQuery(id+"F1.opExtrude","CAP_EDGE",EDGE,{"disambiguationData":[OSD([sQuery(id+"F0.wireOp",EDGE,"E0")])],"isStart":false});var subQ3=makeQuery(id+"F4.imprint","INTERSECT",VERTEX,{"derivedFrom":[subQ1,subQ0]});Q35=makeQuery(id+"F4.imprint","IMPRINT",FACE,{"disambiguationData":[TD([[makeQuery(id+"F4.imprint","IMPRINT",EDGE,{"disambiguationData":[TD([[subQ3,1.0]])],"derivedFrom":subQ0}),1.0]])]});}
            var Q36;
            {var subQ0=sQuery(id+"F4.wireOp",EDGE,"E64");var subQ1=makeQuery(id+"F1.opExtrude","CAP_EDGE",EDGE,{"disambiguationData":[OSD([sQuery(id+"F0.wireOp",EDGE,"E0")])],"isStart":false});var subQ3=makeQuery(id+"F4.imprint","INTERSECT",VERTEX,{"derivedFrom":[subQ1,subQ0]});Q36=makeQuery(id+"F4.imprint","IMPRINT",FACE,{"disambiguationData":[TD([[makeQuery(id+"F4.imprint","IMPRINT",EDGE,{"disambiguationData":[TD([[subQ3,1.0]])],"derivedFrom":subQ0}),1.0]])]});}
            var Q37;
            {var subQ0=sQuery(id+"F4.wireOp",EDGE,"E72");Q37=makeQuery(id+"F4.imprint","IMPRINT",FACE,{"disambiguationData":[TD([[makeQuery(id+"F4.imprint","IMPRINT",EDGE,{"derivedFrom":subQ0}),1.0]])]});}
            var Q38;
            {var subQ0=sQuery(id+"F4.wireOp",EDGE,"E80");Q38=makeQuery(id+"F4.imprint","IMPRINT",FACE,{"disambiguationData":[TD([[makeQuery(id+"F4.imprint","IMPRINT",EDGE,{"derivedFrom":subQ0}),1.0]])]});}
            var Q39;
            {var subQ0=sQuery(id+"F4.wireOp",EDGE,"E88");var subQ1=makeQuery(id+"F1.opExtrude","CAP_EDGE",EDGE,{"disambiguationData":[OSD([sQuery(id+"F0.wireOp",EDGE,"E0")])],"isStart":false});var subQ3=makeQuery(id+"F4.imprint","INTERSECT",VERTEX,{"derivedFrom":[subQ1,subQ0]});Q39=makeQuery(id+"F4.imprint","IMPRINT",FACE,{"disambiguationData":[TD([[makeQuery(id+"F4.imprint","IMPRINT",EDGE,{"disambiguationData":[TD([[subQ3,1.0]])],"derivedFrom":subQ0}),1.0]])]});}
            var Q40;
            {var subQ0=sQuery(id+"F4.wireOp",EDGE,"E96");Q40=makeQuery(id+"F4.imprint","IMPRINT",FACE,{"disambiguationData":[TD([[makeQuery(id+"F4.imprint","IMPRINT",EDGE,{"derivedFrom":subQ0}),1.0]])]});}
            var Q41;
            {var subQ0=sQuery(id+"F4.wireOp",EDGE,"E104");var subQ1=makeQuery(id+"F1.opExtrude","CAP_EDGE",EDGE,{"disambiguationData":[OSD([sQuery(id+"F0.wireOp",EDGE,"E0")])],"isStart":false});var subQ3=makeQuery(id+"F4.imprint","INTERSECT",VERTEX,{"derivedFrom":[subQ1,subQ0]});Q41=makeQuery(id+"F4.imprint","IMPRINT",FACE,{"disambiguationData":[TD([[makeQuery(id+"F4.imprint","IMPRINT",EDGE,{"disambiguationData":[TD([[subQ3,1.0]])],"derivedFrom":subQ0}),1.0]])]});}
            var Q42;
            {var subQ0=sQuery(id+"F4.wireOp",EDGE,"E112");var subQ1=makeQuery(id+"F1.opExtrude","CAP_EDGE",EDGE,{"disambiguationData":[OSD([sQuery(id+"F0.wireOp",EDGE,"E0")])],"isStart":false});var subQ3=makeQuery(id+"F4.imprint","INTERSECT",VERTEX,{"derivedFrom":[subQ1,subQ0]});Q42=makeQuery(id+"F4.imprint","IMPRINT",FACE,{"disambiguationData":[TD([[makeQuery(id+"F4.imprint","IMPRINT",EDGE,{"disambiguationData":[TD([[subQ3,1.0]])],"derivedFrom":subQ0}),1.0]])]});}
            var Q43;
            {var subQ0=sQuery(id+"F4.wireOp",EDGE,"E120");var subQ1=makeQuery(id+"F1.opExtrude","CAP_EDGE",EDGE,{"disambiguationData":[OSD([sQuery(id+"F0.wireOp",EDGE,"E0")])],"isStart":false});var subQ3=makeQuery(id+"F4.imprint","INTERSECT",VERTEX,{"derivedFrom":[subQ1,subQ0]});Q43=makeQuery(id+"F4.imprint","IMPRINT",FACE,{"disambiguationData":[TD([[makeQuery(id+"F4.imprint","IMPRINT",EDGE,{"disambiguationData":[TD([[subQ3,1.0]])],"derivedFrom":subQ0}),1.0]])]});}
            var Q44;
            {var subQ0=sQuery(id+"F4.wireOp",EDGE,"E128");var subQ1=makeQuery(id+"F1.opExtrude","CAP_EDGE",EDGE,{"disambiguationData":[OSD([sQuery(id+"F0.wireOp",EDGE,"E0")])],"isStart":false});var subQ3=makeQuery(id+"F4.imprint","INTERSECT",VERTEX,{"derivedFrom":[subQ1,subQ0]});Q44=makeQuery(id+"F4.imprint","IMPRINT",FACE,{"disambiguationData":[TD([[makeQuery(id+"F4.imprint","IMPRINT",EDGE,{"disambiguationData":[TD([[subQ3,1.0]])],"derivedFrom":subQ0}),1.0]])]});}
            var Q45;
            {var subQ0=sQuery(id+"F4.wireOp",EDGE,"E136");Q45=makeQuery(id+"F4.imprint","IMPRINT",FACE,{"disambiguationData":[TD([[makeQuery(id+"F4.imprint","IMPRINT",EDGE,{"derivedFrom":subQ0}),1.0]])]});}
            var Q46;
            {var subQ0=sQuery(id+"F4.wireOp",EDGE,"E144");Q46=makeQuery(id+"F4.imprint","IMPRINT",FACE,{"disambiguationData":[TD([[makeQuery(id+"F4.imprint","IMPRINT",EDGE,{"derivedFrom":subQ0}),1.0]])]});}
            var Q47;
            {var subQ0=sQuery(id+"F4.wireOp",EDGE,"E152");Q47=makeQuery(id+"F4.imprint","IMPRINT",FACE,{"disambiguationData":[TD([[makeQuery(id+"F4.imprint","IMPRINT",EDGE,{"derivedFrom":subQ0}),1.0]])]});}
            var Q48;
            {var subQ0=sQuery(id+"F4.wireOp",EDGE,"E160");Q48=makeQuery(id+"F4.imprint","IMPRINT",FACE,{"disambiguationData":[TD([[makeQuery(id+"F4.imprint","IMPRINT",EDGE,{"derivedFrom":subQ0}),1.0]])]});}
            var Q49;
            {var subQ0=sQuery(id+"F4.wireOp",EDGE,"E168");Q49=makeQuery(id+"F4.imprint","IMPRINT",FACE,{"disambiguationData":[TD([[makeQuery(id+"F4.imprint","IMPRINT",EDGE,{"derivedFrom":subQ0}),1.0]])]});}
            var Q50;
            Q50=makeQuery(id+"F4.imprint","IMPRINT",FACE,{"disambiguationData":[TD([[makeQuery(id+"F4.imprint","IMPRINT",EDGE,{"derivedFrom":sQuery(id+"F4.wireOp",EDGE,"E176")}),1.0]])]});
            var Q51;
            {var subQ0=sQuery(id+"F4.wireOp",EDGE,"E184");Q51=makeQuery(id+"F4.imprint","IMPRINT",FACE,{"disambiguationData":[TD([[makeQuery(id+"F4.imprint","IMPRINT",EDGE,{"derivedFrom":subQ0}),1.0]])]});}
            var Q52;
            {var subQ0=sQuery(id+"F4.wireOp",EDGE,"E192");Q52=makeQuery(id+"F4.imprint","IMPRINT",FACE,{"disambiguationData":[TD([[makeQuery(id+"F4.imprint","IMPRINT",EDGE,{"derivedFrom":subQ0}),1.0]])]});}
            var Q53;
            {var subQ4=sQuery(id+"F4.wireOp",EDGE,"E200");Q53=makeQuery(id+"F4.imprint","IMPRINT",FACE,{"disambiguationData":[TD([[makeQuery(id+"F4.imprint","IMPRINT",EDGE,{"derivedFrom":subQ4}),1.0]])]});}
            var Q54;
            {var subQ0=sQuery(id+"F4.wireOp",EDGE,"E208");var subQ1=makeQuery(id+"F1.opExtrude","CAP_EDGE",EDGE,{"disambiguationData":[OSD([sQuery(id+"F0.wireOp",EDGE,"E0")])],"isStart":false});var subQ3=makeQuery(id+"F4.imprint","INTERSECT",VERTEX,{"derivedFrom":[subQ1,subQ0]});Q54=makeQuery(id+"F4.imprint","IMPRINT",FACE,{"disambiguationData":[TD([[makeQuery(id+"F4.imprint","IMPRINT",EDGE,{"disambiguationData":[TD([[subQ3,1.0]])],"derivedFrom":subQ0}),1.0]])]});}
            var Q55;
            {var subQ0=sQuery(id+"F4.wireOp",EDGE,"E216");Q55=makeQuery(id+"F4.imprint","IMPRINT",FACE,{"disambiguationData":[TD([[makeQuery(id+"F4.imprint","IMPRINT",EDGE,{"derivedFrom":subQ0}),1.0]])]});}
            var Q56;
            {var subQ0=sQuery(id+"F4.wireOp",EDGE,"E225");Q56=makeQuery(id+"F4.imprint","IMPRINT",FACE,{"disambiguationData":[TD([[makeQuery(id+"F4.imprint","IMPRINT",EDGE,{"derivedFrom":subQ0}),1.0]])]});}
            var Q57;
            {var subQ0=sQuery(id+"F4.wireOp",EDGE,"E233");Q57=makeQuery(id+"F4.imprint","IMPRINT",FACE,{"disambiguationData":[TD([[makeQuery(id+"F4.imprint","IMPRINT",EDGE,{"derivedFrom":subQ0}),1.0]])]});}
            var Q58;
            {var subQ0=sQuery(id+"F4.wireOp",EDGE,"E240");Q58=makeQuery(id+"F4.imprint","IMPRINT",FACE,{"disambiguationData":[TD([[makeQuery(id+"F4.imprint","IMPRINT",EDGE,{"derivedFrom":subQ0}),1.0]])]});}
            var Q59;
            {var subQ2=sQuery(id+"F4.wireOp",EDGE,"E238");Q59=makeQuery(id+"F4.imprint","IMPRINT",FACE,{"disambiguationData":[TD([[makeQuery(id+"F4.imprint","IMPRINT",EDGE,{"derivedFrom":subQ2}),-1.0]])]});}
            extrude(context, id + "F5", {"entities" : qUnion([Q0, Q1, Q2, Q3, Q4, Q5, Q6, Q7, Q8, Q9, Q10, Q11, Q12, Q13, Q14, Q15, Q16, Q17, Q18, Q19, Q20, Q21, Q22, Q23, Q24, Q25, Q26, Q27, Q28, Q29, Q30, Q31, Q32, Q33, Q34, Q35, Q36, Q37, Q38, Q39, Q40, Q41, Q42, Q43, Q44, Q45, Q46, Q47, Q48, Q49, Q50, Q51, Q52, Q53, Q54, Q55, Q56, Q57, Q58, Q59]), "operationType" : NewBodyOperationType.ADD, "oppositeDirection" : true, "depth" : 12.7 * mm});
        }
        {
            var Q0;
            Q0=makeQuery(id+"F5.boolean.opBoolean","MERGE",FACE,{"derivedFrom":[makeQuery(id+"F1.opExtrude","CAP_FACE",FACE,{"disambiguationData":[OSD([sQuery(id+"F0.wireOp",EDGE,"E0"),sQuery(id+"F0.wireOp",EDGE,"E1")])],"isStart":false}),makeQuery(id+"F5.opExtrude","CAP_FACE",FACE,{"disambiguationData":[OSD([sQuery(id+"F4.wireOp",EDGE,"E5"),sQuery(id+"F4.wireOp",EDGE,"E6"),sQuery(id+"F4.wireOp",EDGE,"E7"),sQuery(id+"F4.wireOp",EDGE,"E8"),sQuery(id+"F4.wireOp",EDGE,"E9.filletArc"),sQuery(id+"F4.wireOp",EDGE,"E10.filletArc"),sQuery(id+"F4.wireOp",EDGE,"E11.filletArc")])],"isStart":true}),makeQuery(id+"F5.opExtrude","CAP_FACE",FACE,{"disambiguationData":[OSD([sQuery(id+"F4.wireOp",EDGE,"E13"),sQuery(id+"F4.wireOp",EDGE,"E14"),sQuery(id+"F4.wireOp",EDGE,"E15"),sQuery(id+"F4.wireOp",EDGE,"E16"),sQuery(id+"F4.wireOp",EDGE,"E17.filletArc"),sQuery(id+"F4.wireOp",EDGE,"E18.filletArc"),sQuery(id+"F4.wireOp",EDGE,"E19.filletArc")])],"isStart":true}),makeQuery(id+"F5.opExtrude","CAP_FACE",FACE,{"disambiguationData":[OSD([sQuery(id+"F4.wireOp",EDGE,"E21"),sQuery(id+"F4.wireOp",EDGE,"E22"),sQuery(id+"F4.wireOp",EDGE,"E23"),sQuery(id+"F4.wireOp",EDGE,"E24"),sQuery(id+"F4.wireOp",EDGE,"E25.filletArc"),sQuery(id+"F4.wireOp",EDGE,"E26.filletArc"),sQuery(id+"F4.wireOp",EDGE,"E27.filletArc")])],"isStart":true}),makeQuery(id+"F5.opExtrude","CAP_FACE",FACE,{"disambiguationData":[OSD([sQuery(id+"F4.wireOp",EDGE,"E29"),sQuery(id+"F4.wireOp",EDGE,"E30"),sQuery(id+"F4.wireOp",EDGE,"E31"),sQuery(id+"F4.wireOp",EDGE,"E32"),sQuery(id+"F4.wireOp",EDGE,"E33.filletArc"),sQuery(id+"F4.wireOp",EDGE,"E34.filletArc"),sQuery(id+"F4.wireOp",EDGE,"E35.filletArc")])],"isStart":true}),makeQuery(id+"F5.opExtrude","CAP_FACE",FACE,{"disambiguationData":[OSD([sQuery(id+"F4.wireOp",EDGE,"E37"),sQuery(id+"F4.wireOp",EDGE,"E38"),sQuery(id+"F4.wireOp",EDGE,"E39"),sQuery(id+"F4.wireOp",EDGE,"E40"),sQuery(id+"F4.wireOp",EDGE,"E41.filletArc"),sQuery(id+"F4.wireOp",EDGE,"E42.filletArc"),sQuery(id+"F4.wireOp",EDGE,"E43.filletArc")])],"isStart":true}),makeQuery(id+"F5.opExtrude","CAP_FACE",FACE,{"disambiguationData":[OSD([sQuery(id+"F4.wireOp",EDGE,"E45"),sQuery(id+"F4.wireOp",EDGE,"E46"),sQuery(id+"F4.wireOp",EDGE,"E47"),sQuery(id+"F4.wireOp",EDGE,"E48"),sQuery(id+"F4.wireOp",EDGE,"E49.filletArc"),sQuery(id+"F4.wireOp",EDGE,"E50.filletArc"),sQuery(id+"F4.wireOp",EDGE,"E51.filletArc")])],"isStart":true}),makeQuery(id+"F5.opExtrude","CAP_FACE",FACE,{"disambiguationData":[OSD([sQuery(id+"F4.wireOp",EDGE,"E53"),sQuery(id+"F4.wireOp",EDGE,"E54"),sQuery(id+"F4.wireOp",EDGE,"E55"),sQuery(id+"F4.wireOp",EDGE,"E56"),sQuery(id+"F4.wireOp",EDGE,"E57.filletArc"),sQuery(id+"F4.wireOp",EDGE,"E58.filletArc"),sQuery(id+"F4.wireOp",EDGE,"E59.filletArc")])],"isStart":true}),makeQuery(id+"F5.opExtrude","CAP_FACE",FACE,{"disambiguationData":[OSD([sQuery(id+"F4.wireOp",EDGE,"E61"),sQuery(id+"F4.wireOp",EDGE,"E62"),sQuery(id+"F4.wireOp",EDGE,"E63"),sQuery(id+"F4.wireOp",EDGE,"E64"),sQuery(id+"F4.wireOp",EDGE,"E65.filletArc"),sQuery(id+"F4.wireOp",EDGE,"E66.filletArc"),sQuery(id+"F4.wireOp",EDGE,"E67.filletArc")])],"isStart":true}),makeQuery(id+"F5.opExtrude","CAP_FACE",FACE,{"disambiguationData":[OSD([sQuery(id+"F4.wireOp",EDGE,"E69"),sQuery(id+"F4.wireOp",EDGE,"E70"),sQuery(id+"F4.wireOp",EDGE,"E71"),sQuery(id+"F4.wireOp",EDGE,"E72"),sQuery(id+"F4.wireOp",EDGE,"E73.filletArc"),sQuery(id+"F4.wireOp",EDGE,"E74.filletArc"),sQuery(id+"F4.wireOp",EDGE,"E75.filletArc")])],"isStart":true}),makeQuery(id+"F5.opExtrude","CAP_FACE",FACE,{"disambiguationData":[OSD([sQuery(id+"F4.wireOp",EDGE,"E77"),sQuery(id+"F4.wireOp",EDGE,"E78"),sQuery(id+"F4.wireOp",EDGE,"E79"),sQuery(id+"F4.wireOp",EDGE,"E80"),sQuery(id+"F4.wireOp",EDGE,"E81.filletArc"),sQuery(id+"F4.wireOp",EDGE,"E82.filletArc"),sQuery(id+"F4.wireOp",EDGE,"E83.filletArc")])],"isStart":true}),makeQuery(id+"F5.opExtrude","CAP_FACE",FACE,{"disambiguationData":[OSD([sQuery(id+"F4.wireOp",EDGE,"E85"),sQuery(id+"F4.wireOp",EDGE,"E86"),sQuery(id+"F4.wireOp",EDGE,"E87"),sQuery(id+"F4.wireOp",EDGE,"E88"),sQuery(id+"F4.wireOp",EDGE,"E89.filletArc"),sQuery(id+"F4.wireOp",EDGE,"E90.filletArc"),sQuery(id+"F4.wireOp",EDGE,"E91.filletArc")])],"isStart":true}),makeQuery(id+"F5.opExtrude","CAP_FACE",FACE,{"disambiguationData":[OSD([sQuery(id+"F4.wireOp",EDGE,"E93"),sQuery(id+"F4.wireOp",EDGE,"E94"),sQuery(id+"F4.wireOp",EDGE,"E95"),sQuery(id+"F4.wireOp",EDGE,"E96"),sQuery(id+"F4.wireOp",EDGE,"E97.filletArc"),sQuery(id+"F4.wireOp",EDGE,"E98.filletArc"),sQuery(id+"F4.wireOp",EDGE,"E99.filletArc")])],"isStart":true}),makeQuery(id+"F5.opExtrude","CAP_FACE",FACE,{"disambiguationData":[OSD([sQuery(id+"F4.wireOp",EDGE,"E101"),sQuery(id+"F4.wireOp",EDGE,"E102"),sQuery(id+"F4.wireOp",EDGE,"E103"),sQuery(id+"F4.wireOp",EDGE,"E104"),sQuery(id+"F4.wireOp",EDGE,"E105.filletArc"),sQuery(id+"F4.wireOp",EDGE,"E106.filletArc"),sQuery(id+"F4.wireOp",EDGE,"E107.filletArc")])],"isStart":true}),makeQuery(id+"F5.opExtrude","CAP_FACE",FACE,{"disambiguationData":[OSD([sQuery(id+"F4.wireOp",EDGE,"E109"),sQuery(id+"F4.wireOp",EDGE,"E110"),sQuery(id+"F4.wireOp",EDGE,"E111"),sQuery(id+"F4.wireOp",EDGE,"E112"),sQuery(id+"F4.wireOp",EDGE,"E113.filletArc"),sQuery(id+"F4.wireOp",EDGE,"E114.filletArc"),sQuery(id+"F4.wireOp",EDGE,"E115.filletArc")])],"isStart":true}),makeQuery(id+"F5.opExtrude","CAP_FACE",FACE,{"disambiguationData":[OSD([sQuery(id+"F4.wireOp",EDGE,"E117"),sQuery(id+"F4.wireOp",EDGE,"E118"),sQuery(id+"F4.wireOp",EDGE,"E119"),sQuery(id+"F4.wireOp",EDGE,"E120"),sQuery(id+"F4.wireOp",EDGE,"E121.filletArc"),sQuery(id+"F4.wireOp",EDGE,"E122.filletArc"),sQuery(id+"F4.wireOp",EDGE,"E123.filletArc")])],"isStart":true}),makeQuery(id+"F5.opExtrude","CAP_FACE",FACE,{"disambiguationData":[OSD([sQuery(id+"F4.wireOp",EDGE,"E125"),sQuery(id+"F4.wireOp",EDGE,"E126"),sQuery(id+"F4.wireOp",EDGE,"E127"),sQuery(id+"F4.wireOp",EDGE,"E128"),sQuery(id+"F4.wireOp",EDGE,"E129.filletArc"),sQuery(id+"F4.wireOp",EDGE,"E130.filletArc"),sQuery(id+"F4.wireOp",EDGE,"E131.filletArc")])],"isStart":true}),makeQuery(id+"F5.opExtrude","CAP_FACE",FACE,{"disambiguationData":[OSD([sQuery(id+"F4.wireOp",EDGE,"E133"),sQuery(id+"F4.wireOp",EDGE,"E134"),sQuery(id+"F4.wireOp",EDGE,"E135"),sQuery(id+"F4.wireOp",EDGE,"E136"),sQuery(id+"F4.wireOp",EDGE,"E137.filletArc"),sQuery(id+"F4.wireOp",EDGE,"E138.filletArc"),sQuery(id+"F4.wireOp",EDGE,"E139.filletArc")])],"isStart":true}),makeQuery(id+"F5.opExtrude","CAP_FACE",FACE,{"disambiguationData":[OSD([sQuery(id+"F4.wireOp",EDGE,"E141"),sQuery(id+"F4.wireOp",EDGE,"E142"),sQuery(id+"F4.wireOp",EDGE,"E143"),sQuery(id+"F4.wireOp",EDGE,"E144"),sQuery(id+"F4.wireOp",EDGE,"E145.filletArc"),sQuery(id+"F4.wireOp",EDGE,"E146.filletArc"),sQuery(id+"F4.wireOp",EDGE,"E147.filletArc")])],"isStart":true}),makeQuery(id+"F5.opExtrude","CAP_FACE",FACE,{"disambiguationData":[OSD([sQuery(id+"F4.wireOp",EDGE,"E149"),sQuery(id+"F4.wireOp",EDGE,"E150"),sQuery(id+"F4.wireOp",EDGE,"E151"),sQuery(id+"F4.wireOp",EDGE,"E152"),sQuery(id+"F4.wireOp",EDGE,"E153.filletArc"),sQuery(id+"F4.wireOp",EDGE,"E154.filletArc"),sQuery(id+"F4.wireOp",EDGE,"E155.filletArc")])],"isStart":true}),makeQuery(id+"F5.opExtrude","CAP_FACE",FACE,{"disambiguationData":[OSD([sQuery(id+"F4.wireOp",EDGE,"E157"),sQuery(id+"F4.wireOp",EDGE,"E158"),sQuery(id+"F4.wireOp",EDGE,"E159"),sQuery(id+"F4.wireOp",EDGE,"E160"),sQuery(id+"F4.wireOp",EDGE,"E161.filletArc"),sQuery(id+"F4.wireOp",EDGE,"E162.filletArc"),sQuery(id+"F4.wireOp",EDGE,"E163.filletArc")])],"isStart":true}),makeQuery(id+"F5.opExtrude","CAP_FACE",FACE,{"disambiguationData":[OSD([sQuery(id+"F4.wireOp",EDGE,"E165"),sQuery(id+"F4.wireOp",EDGE,"E166"),sQuery(id+"F4.wireOp",EDGE,"E167"),sQuery(id+"F4.wireOp",EDGE,"E168"),sQuery(id+"F4.wireOp",EDGE,"E169.filletArc"),sQuery(id+"F4.wireOp",EDGE,"E170.filletArc"),sQuery(id+"F4.wireOp",EDGE,"E171.filletArc")])],"isStart":true}),makeQuery(id+"F5.opExtrude","CAP_FACE",FACE,{"disambiguationData":[OSD([sQuery(id+"F4.wireOp",EDGE,"E173"),sQuery(id+"F4.wireOp",EDGE,"E174"),sQuery(id+"F4.wireOp",EDGE,"E175"),sQuery(id+"F4.wireOp",EDGE,"E176"),sQuery(id+"F4.wireOp",EDGE,"E177.filletArc"),sQuery(id+"F4.wireOp",EDGE,"E178.filletArc"),sQuery(id+"F4.wireOp",EDGE,"E179.filletArc")])],"isStart":true}),makeQuery(id+"F5.opExtrude","CAP_FACE",FACE,{"disambiguationData":[OSD([sQuery(id+"F4.wireOp",EDGE,"E181"),sQuery(id+"F4.wireOp",EDGE,"E182"),sQuery(id+"F4.wireOp",EDGE,"E183"),sQuery(id+"F4.wireOp",EDGE,"E184"),sQuery(id+"F4.wireOp",EDGE,"E185.filletArc"),sQuery(id+"F4.wireOp",EDGE,"E186.filletArc"),sQuery(id+"F4.wireOp",EDGE,"E187.filletArc")])],"isStart":true}),makeQuery(id+"F5.opExtrude","CAP_FACE",FACE,{"disambiguationData":[OSD([sQuery(id+"F4.wireOp",EDGE,"E189"),sQuery(id+"F4.wireOp",EDGE,"E190"),sQuery(id+"F4.wireOp",EDGE,"E191"),sQuery(id+"F4.wireOp",EDGE,"E192"),sQuery(id+"F4.wireOp",EDGE,"E193.filletArc"),sQuery(id+"F4.wireOp",EDGE,"E194.filletArc"),sQuery(id+"F4.wireOp",EDGE,"E195.filletArc")])],"isStart":true}),makeQuery(id+"F5.opExtrude","CAP_FACE",FACE,{"disambiguationData":[OSD([sQuery(id+"F4.wireOp",EDGE,"E197"),sQuery(id+"F4.wireOp",EDGE,"E198"),sQuery(id+"F4.wireOp",EDGE,"E199"),sQuery(id+"F4.wireOp",EDGE,"E200"),sQuery(id+"F4.wireOp",EDGE,"E201.filletArc"),sQuery(id+"F4.wireOp",EDGE,"E202.filletArc"),sQuery(id+"F4.wireOp",EDGE,"E203.filletArc")])],"isStart":true}),makeQuery(id+"F5.opExtrude","CAP_FACE",FACE,{"disambiguationData":[OSD([sQuery(id+"F4.wireOp",EDGE,"E205"),sQuery(id+"F4.wireOp",EDGE,"E206"),sQuery(id+"F4.wireOp",EDGE,"E207"),sQuery(id+"F4.wireOp",EDGE,"E208"),sQuery(id+"F4.wireOp",EDGE,"E209.filletArc"),sQuery(id+"F4.wireOp",EDGE,"E210.filletArc"),sQuery(id+"F4.wireOp",EDGE,"E211.filletArc")])],"isStart":true}),makeQuery(id+"F5.opExtrude","CAP_FACE",FACE,{"disambiguationData":[OSD([sQuery(id+"F4.wireOp",EDGE,"E213"),sQuery(id+"F4.wireOp",EDGE,"E214"),sQuery(id+"F4.wireOp",EDGE,"E215"),sQuery(id+"F4.wireOp",EDGE,"E216"),sQuery(id+"F4.wireOp",EDGE,"E217.filletArc"),sQuery(id+"F4.wireOp",EDGE,"E218.filletArc"),sQuery(id+"F4.wireOp",EDGE,"E219.filletArc")])],"isStart":true}),makeQuery(id+"F5.opExtrude","CAP_FACE",FACE,{"disambiguationData":[OSD([sQuery(id+"F4.wireOp",EDGE,"E222"),sQuery(id+"F4.wireOp",EDGE,"E223"),sQuery(id+"F4.wireOp",EDGE,"E224"),sQuery(id+"F4.wireOp",EDGE,"E225"),sQuery(id+"F4.wireOp",EDGE,"E226.filletArc"),sQuery(id+"F4.wireOp",EDGE,"E227.filletArc"),sQuery(id+"F4.wireOp",EDGE,"E228.filletArc")])],"isStart":true}),makeQuery(id+"F5.opExtrude","CAP_FACE",FACE,{"disambiguationData":[OSD([sQuery(id+"F4.wireOp",EDGE,"E230"),sQuery(id+"F4.wireOp",EDGE,"E231"),sQuery(id+"F4.wireOp",EDGE,"E232"),sQuery(id+"F4.wireOp",EDGE,"E233"),sQuery(id+"F4.wireOp",EDGE,"E234.filletArc"),sQuery(id+"F4.wireOp",EDGE,"E235.filletArc"),sQuery(id+"F4.wireOp",EDGE,"E236.filletArc")])],"isStart":true}),makeQuery(id+"F5.opExtrude","CAP_FACE",FACE,{"disambiguationData":[OSD([sQuery(id+"F4.wireOp",EDGE,"E237"),sQuery(id+"F4.wireOp",EDGE,"E238"),sQuery(id+"F4.wireOp",EDGE,"E239"),sQuery(id+"F4.wireOp",EDGE,"E240"),sQuery(id+"F4.wireOp",EDGE,"E241.filletArc"),sQuery(id+"F4.wireOp",EDGE,"E242.filletArc"),sQuery(id+"F4.wireOp",EDGE,"E243.filletArc")])],"isStart":true})]});
            var sketch = newSketch(context, id + "F6", { "sketchPlane" : qUnion([Q0])});
            skLineSegment(sketch, "E246", {"start": v(-63.58, 70.13) * mm, "end": v(-65.47, 70.13) * mm});
            skLineSegment(sketch, "E247", {"start": v(-65.47, 70.13) * mm, "end": v(-62.21, 70.13) * mm});
            skLineSegment(sketch, "E248", {"start": v(-61.59, 69.62) * mm, "end": v(-60.81, 65.52) * mm});
            skLineSegment(sketch, "E249", {"start": v(-65.47, 70.13) * mm, "end": v(-66.41, 65.52) * mm});
            skLineSegment(sketch, "E250", {"start": v(-65.79, 64.76) * mm, "end": v(-61.44, 64.76) * mm});
            skArc(sketch, "E251.filletArc", {"start": v(-61.59, 69.62) * mm, "mid": v(-61.8, 69.99) * mm, "end": v(-62.21, 70.13) * mm});
            skArc(sketch, "E252.filletArc", {"start": v(-61.44, 64.76) * mm, "mid": v(-60.95, 65) * mm, "end": v(-60.81, 65.52) * mm});
            skArc(sketch, "E253.filletArc", {"start": v(-66.41, 65.52) * mm, "mid": v(-66.28, 65) * mm, "end": v(-65.79, 64.76) * mm});
            skLineSegment(sketch, "E254", {"start": v(-50.87, 66.4) * mm, "end": v(-52.45, 67.42) * mm});
            skLineSegment(sketch, "E255", {"start": v(-52.45, 67.42) * mm, "end": v(-49.72, 65.66) * mm});
            skLineSegment(sketch, "E256", {"start": v(-49.47, 64.89) * mm, "end": v(-51.04, 61.02) * mm});
            skLineSegment(sketch, "E257", {"start": v(-52.45, 67.42) * mm, "end": v(-55.74, 64.06) * mm});
            skLineSegment(sketch, "E258", {"start": v(-55.63, 63.08) * mm, "end": v(-51.97, 60.72) * mm});
            skArc(sketch, "E259.filletArc", {"start": v(-49.47, 64.89) * mm, "mid": v(-49.46, 65.32) * mm, "end": v(-49.72, 65.66) * mm});
            skArc(sketch, "E260.filletArc", {"start": v(-51.97, 60.72) * mm, "mid": v(-51.43, 60.65) * mm, "end": v(-51.04, 61.02) * mm});
            skArc(sketch, "E261.filletArc", {"start": v(-55.74, 64.06) * mm, "mid": v(-55.92, 63.54) * mm, "end": v(-55.63, 63.08) * mm});
            skLineSegment(sketch, "E262", {"start": v(-42.1, 56.94) * mm, "end": v(-43.05, 58.57) * mm});
            skLineSegment(sketch, "E263", {"start": v(-43.05, 58.57) * mm, "end": v(-41.42, 55.75) * mm});
            skLineSegment(sketch, "E264", {"start": v(-41.56, 54.95) * mm, "end": v(-44.72, 52.23) * mm});
            skLineSegment(sketch, "E265", {"start": v(-43.05, 58.57) * mm, "end": v(-47.51, 57.08) * mm});
            skLineSegment(sketch, "E266", {"start": v(-47.86, 56.16) * mm, "end": v(-45.68, 52.4) * mm});
            skArc(sketch, "E267.filletArc", {"start": v(-41.56, 54.95) * mm, "mid": v(-41.34, 55.33) * mm, "end": v(-41.42, 55.75) * mm});
            skArc(sketch, "E268.filletArc", {"start": v(-45.68, 52.4) * mm, "mid": v(-45.24, 52.09) * mm, "end": v(-44.72, 52.23) * mm});
            skArc(sketch, "E269.filletArc", {"start": v(-47.51, 57.08) * mm, "mid": v(-47.9, 56.7) * mm, "end": v(-47.86, 56.16) * mm});
            skLineSegment(sketch, "E270", {"start": v(-39.64, 43.7) * mm, "end": v(-39.48, 45.57) * mm});
            skLineSegment(sketch, "E271", {"start": v(-39.48, 45.57) * mm, "end": v(-39.76, 42.33) * mm});
            skLineSegment(sketch, "E272", {"start": v(-40.33, 41.76) * mm, "end": v(-44.48, 41.34) * mm});
            skLineSegment(sketch, "E273", {"start": v(-39.48, 45.57) * mm, "end": v(-43.99, 46.92) * mm});
            skLineSegment(sketch, "E274", {"start": v(-44.8, 46.36) * mm, "end": v(-45.18, 42.03) * mm});
            skArc(sketch, "E275.filletArc", {"start": v(-40.33, 41.76) * mm, "mid": v(-39.94, 41.94) * mm, "end": v(-39.76, 42.33) * mm});
            skArc(sketch, "E276.filletArc", {"start": v(-45.18, 42.03) * mm, "mid": v(-44.99, 41.52) * mm, "end": v(-44.48, 41.34) * mm});
            skArc(sketch, "E277.filletArc", {"start": v(-43.99, 46.92) * mm, "mid": v(-44.53, 46.83) * mm, "end": v(-44.8, 46.36) * mm});
            skSolve(sketch);
        }
        {
            var Q0;
            Q0 = qSketchRegion(id + "F6", true);
            extrude(context, id + "F7", {"entities" : qUnion([Q0]), "operationType" : NewBodyOperationType.ADD, "oppositeDirection" : true, "depth" : 12.7 * mm});
        }
    });
